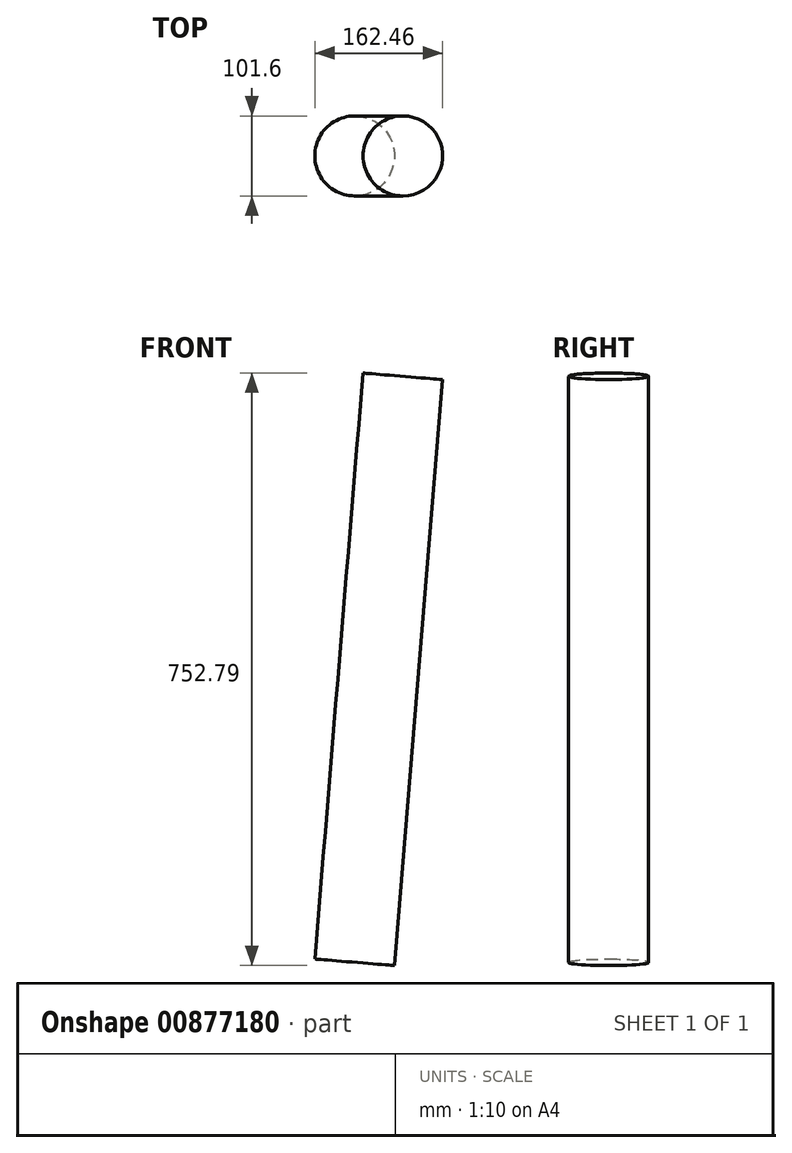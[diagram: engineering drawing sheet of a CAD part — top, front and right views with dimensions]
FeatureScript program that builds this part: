
annotation { "Feature Type Name" : "Feature", "Feature Type Description" : "" }
export const myFeature = defineFeature(function(context is Context, id is Id, definition is map)
    precondition{}
    {
        {
            var Q0;
            Q0=qCreatedBy(makeId("Front.planeOp"),FACE);
            var sketch = newSketch(context, id + "F0", { "sketchPlane" : qUnion([Q0])});
            skCircle(sketch, "E0", {"center": v(-177.37, -501.7) * mm, "radius": 120.6 * mm});
            skLineSegment(sketch, "E1", {"start": v(0, 0) * mm, "end": v(-124.43, 117.5) * mm});
            skLineSegment(sketch, "E2", {"start": v(-124.43, 117.5) * mm, "end": v(-179.9, -381.13) * mm});
            skLineSegment(sketch, "E3", {"start": v(0, 0) * mm, "end": v(219.53, -68.62) * mm});
            skLineSegment(sketch, "E4", {"start": v(213.8, -138.23) * mm, "end": v(152.6, -882.7) * mm});
            skLineSegment(sketch, "E5", {"start": v(213.8, -138.23) * mm, "end": v(219.53, -68.62) * mm});
            skCircle(sketch, "E6", {"center": v(0, 0) * mm, "radius": 31.75 * mm});
            skLineSegment(sketch, "E7", {"start": v(0, 0) * mm, "end": v(0, -326.21) * mm});
            skLineSegment(sketch, "E8", {"start": v(0, 0) * mm, "end": v(750.1, 2.92) * mm});
            skSolve(sketch);
        }
        {
            var Q0;
            Q0=sQuery(id+"F0.wireOp",EDGE,"E4");
            var Q1;
            Q1=qBodyType(qCreatedBy(id+"F2",EDGE),BodyType.WIRE);
            cPlane(context, id + "F1", {"entities" : qUnion([Q0, Q1]), "cplaneType" : CPlaneType.MID_PLANE, "offset" : 25 * mm, "width" : 150 * mm, "height" : 150 * mm});
        }
        {
            var Q0;
            Q0=qCreatedBy(id+"F1.planeOp",FACE);
            var sketch = newSketch(context, id + "F2", { "sketchPlane" : qUnion([Q0])});
            skCircle(sketch, "E9", {"center": v(224.4, 0) * mm, "radius": 50.8 * mm});
            skSolve(sketch);
        }
        {
            var Q0;
            Q0=makeQuery(id+"F2.imprint","IMPRINT",FACE,{"disambiguationData":[TD([[makeQuery(id+"F2.imprint","IMPRINT",EDGE,{"derivedFrom":sQuery(id+"F2.wireOp",EDGE,"E9")}),1.0]])]});
            var Q1;
            Q1=sQuery(id+"F0.wireOp",EDGE,"E4");
            sweep(context, id + "F3", {"profiles" : qUnion([Q0]), "path" : qUnion([Q1])});
        }
    });
